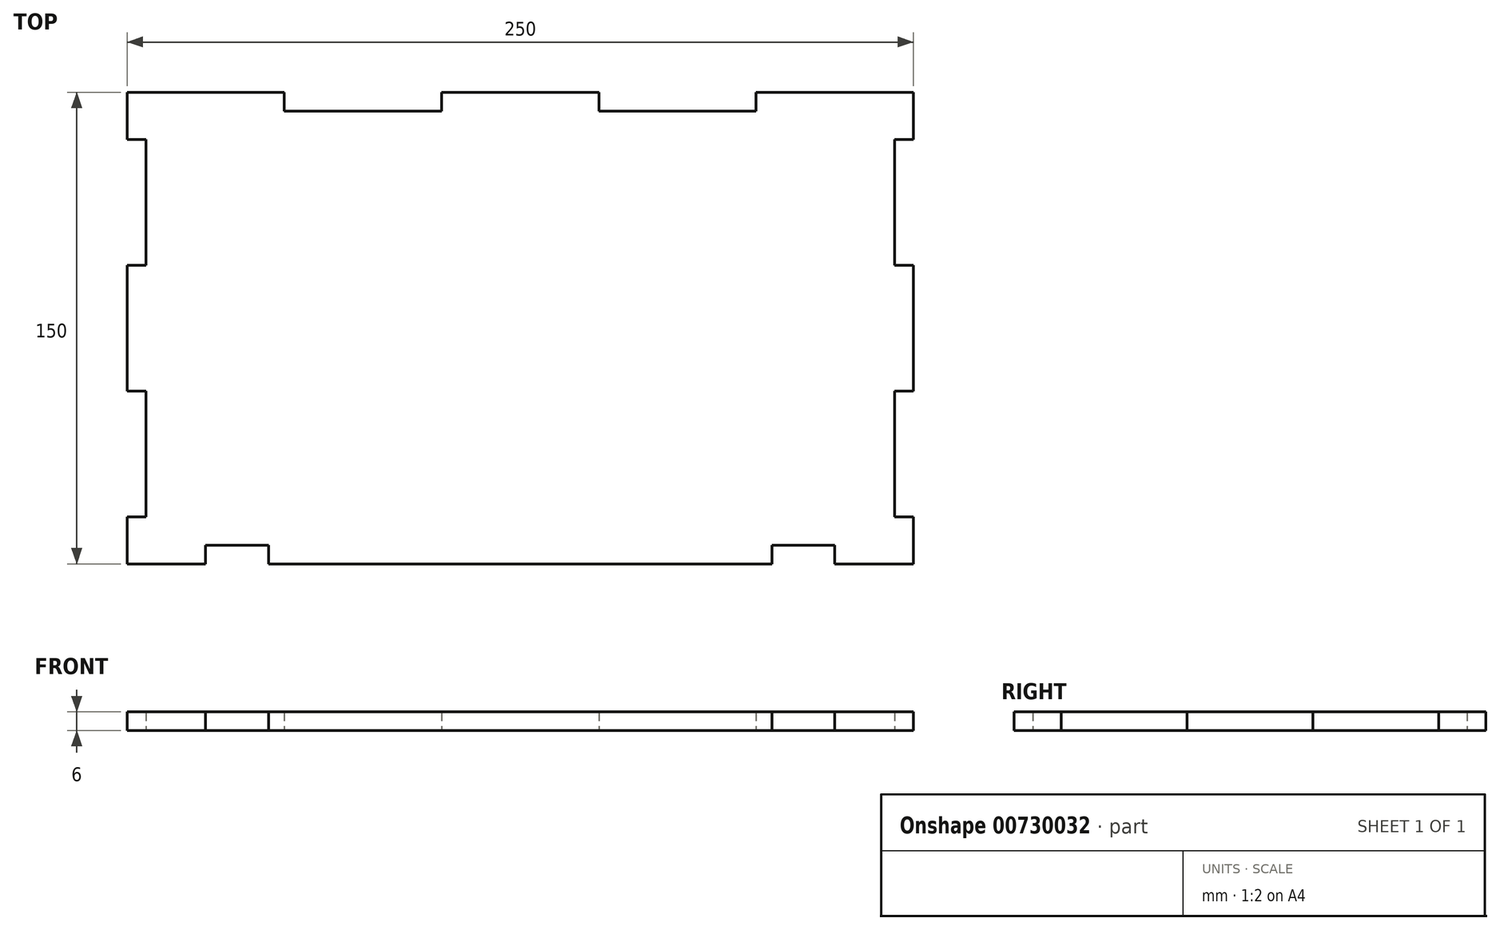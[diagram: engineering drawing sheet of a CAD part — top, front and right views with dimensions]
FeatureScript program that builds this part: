
annotation { "Feature Type Name" : "Feature", "Feature Type Description" : "" }
export const myFeature = defineFeature(function(context is Context, id is Id, definition is map)
    precondition{}
    {
        {
            var Q0;
            Q0=qCreatedBy(makeId("Top.planeOp"),FACE);
            var sketch = newSketch(context, id + "F0", { "sketchPlane" : qUnion([Q0])});
            skLineSegment(sketch, "E0", {"start": v(-64.48, -59.73) * mm, "end": v(-39.48, -59.73) * mm});
            skLineSegment(sketch, "E1", {"start": v(-64.48, -59.73) * mm, "end": v(-64.48, -44.73) * mm});
            skLineSegment(sketch, "E2", {"start": v(-64.48, -44.73) * mm, "end": v(-58.48, -44.73) * mm});
            skLineSegment(sketch, "E3", {"start": v(-58.48, -44.73) * mm, "end": v(-58.48, -4.73) * mm});
            skLineSegment(sketch, "E4", {"start": v(-58.48, -4.73) * mm, "end": v(-64.48, -4.73) * mm});
            skLineSegment(sketch, "E5", {"start": v(-64.48, -4.73) * mm, "end": v(-64.48, 35.27) * mm});
            skLineSegment(sketch, "E6", {"start": v(-64.48, 35.27) * mm, "end": v(-58.48, 35.27) * mm});
            skLineSegment(sketch, "E7", {"start": v(-58.48, 35.27) * mm, "end": v(-58.48, 75.27) * mm});
            skLineSegment(sketch, "E8", {"start": v(-58.48, 75.27) * mm, "end": v(-64.48, 75.27) * mm});
            skLineSegment(sketch, "E9", {"start": v(-64.48, 75.27) * mm, "end": v(-64.48, 90.27) * mm});
            skLineSegment(sketch, "E10", {"start": v(-64.48, 90.27) * mm, "end": v(-14.48, 90.27) * mm});
            skLineSegment(sketch, "E11", {"start": v(-14.48, 90.27) * mm, "end": v(-14.48, 84.27) * mm});
            skLineSegment(sketch, "E12", {"start": v(-14.48, 84.27) * mm, "end": v(35.52, 84.27) * mm});
            skLineSegment(sketch, "E13", {"start": v(35.52, 84.27) * mm, "end": v(35.52, 90.27) * mm});
            skLineSegment(sketch, "E14", {"start": v(35.52, 90.27) * mm, "end": v(85.52, 90.27) * mm});
            skLineSegment(sketch, "E15", {"start": v(85.52, 90.27) * mm, "end": v(85.52, 84.27) * mm});
            skLineSegment(sketch, "E16", {"start": v(85.52, 84.27) * mm, "end": v(135.52, 84.27) * mm});
            skLineSegment(sketch, "E17", {"start": v(135.52, 84.27) * mm, "end": v(135.52, 90.27) * mm});
            skLineSegment(sketch, "E18", {"start": v(135.52, 90.27) * mm, "end": v(185.52, 90.27) * mm});
            skLineSegment(sketch, "E19", {"start": v(185.52, 90.27) * mm, "end": v(185.52, 75.27) * mm});
            skLineSegment(sketch, "E20", {"start": v(185.52, 75.27) * mm, "end": v(179.52, 75.27) * mm});
            skLineSegment(sketch, "E21", {"start": v(179.52, 75.27) * mm, "end": v(179.52, 35.27) * mm});
            skLineSegment(sketch, "E22", {"start": v(179.52, 35.27) * mm, "end": v(185.52, 35.27) * mm});
            skLineSegment(sketch, "E23", {"start": v(185.52, 35.27) * mm, "end": v(185.52, -4.73) * mm});
            skLineSegment(sketch, "E24", {"start": v(185.52, -4.73) * mm, "end": v(179.52, -4.73) * mm});
            skLineSegment(sketch, "E25", {"start": v(179.52, -4.73) * mm, "end": v(179.52, -44.73) * mm});
            skLineSegment(sketch, "E26", {"start": v(179.52, -44.73) * mm, "end": v(185.52, -44.73) * mm});
            skLineSegment(sketch, "E27", {"start": v(185.52, -44.73) * mm, "end": v(185.52, -59.73) * mm});
            skLineSegment(sketch, "E28", {"start": v(-39.48, -59.73) * mm, "end": v(-39.48, -53.73) * mm});
            skLineSegment(sketch, "E29", {"start": v(-39.48, -53.73) * mm, "end": v(-19.48, -53.73) * mm});
            skLineSegment(sketch, "E30", {"start": v(-19.48, -53.73) * mm, "end": v(-19.48, -59.73) * mm});
            skLineSegment(sketch, "E31", {"start": v(185.52, -59.73) * mm, "end": v(160.52, -59.73) * mm});
            skLineSegment(sketch, "E32", {"start": v(160.52, -59.73) * mm, "end": v(160.52, -53.73) * mm});
            skLineSegment(sketch, "E33", {"start": v(160.52, -53.73) * mm, "end": v(140.52, -53.73) * mm});
            skLineSegment(sketch, "E34", {"start": v(140.52, -53.73) * mm, "end": v(140.52, -59.73) * mm});
            skLineSegment(sketch, "E35", {"start": v(-19.48, -59.73) * mm, "end": v(140.52, -59.73) * mm});
            skSolve(sketch);
        }
        {
            var Q0;
            Q0 = qSketchRegion(id + "F0", true);
            extrude(context, id + "F1", {"entities" : qUnion([Q0]), "depth" : 6 * mm, "offsetDistance" : 25 * mm});
        }
    });
